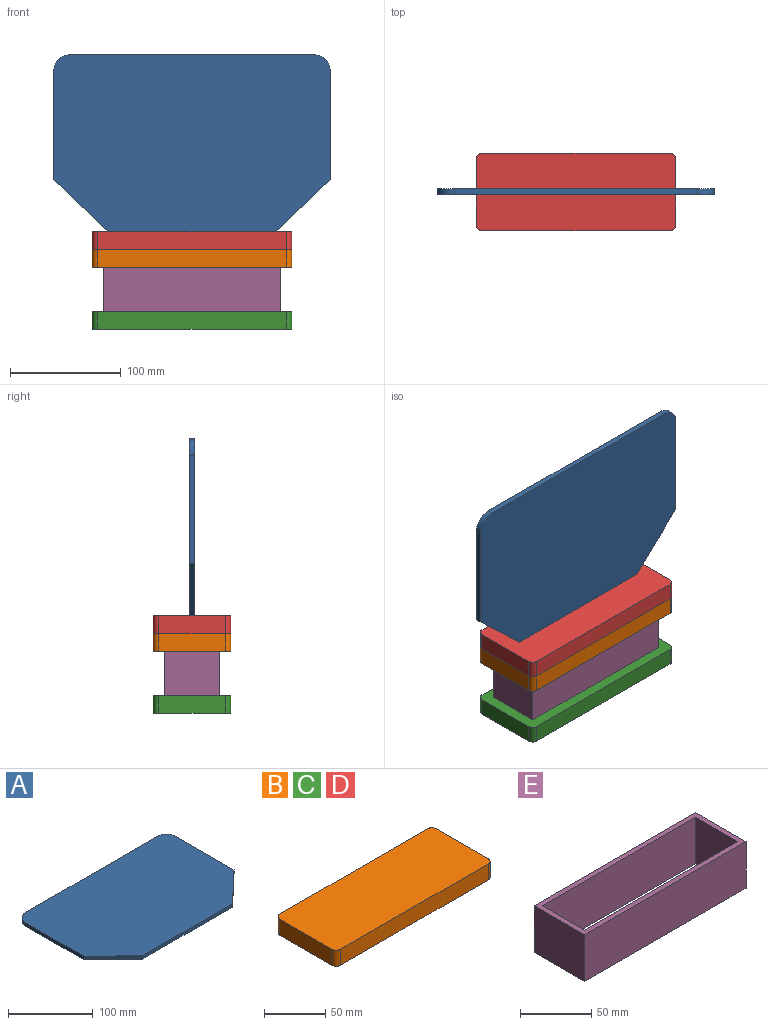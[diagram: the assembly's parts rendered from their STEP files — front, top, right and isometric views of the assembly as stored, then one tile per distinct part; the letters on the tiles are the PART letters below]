
ASSEMBLY  parts=5 mates=4
PART A: 10 faces, bbox 250x160x5 mm
  f0: plane 50x47.5mm, normal (-0.69,-0.72,0), area 344.8mm2, adj f1,f7,f8,f9
  f1: plane 150x5mm, normal (0,-1,0), area 750mm2, adj f0,f2,f8,f9
  f2: plane 50x47.5mm, normal (0.69,-0.72,0), area 344.8mm2, adj f1,f3,f8,f9
  f3: plane 97.5x5mm, normal (1,0,0), area 487.5mm2, adj f2,f4,f8,f9
  f4: cylinder r=15mm len=15mm, axis (0,0,-1), area 117.8mm2, adj f3,f5,f8,f9
  f5: plane 220x5mm, normal (0,1,0), area 1100mm2, adj f4,f6,f8,f9
  f6: cylinder r=15mm len=15mm, axis (0,0,-1), area 117.8mm2, adj f5,f7,f8,f9
  f7: plane 97.5x5mm, normal (-1,0,0), area 487.5mm2, adj f0,f6,f8,f9
  f8: plane 250x160mm, normal (0,0,1), area 37528.3mm2, adj f0,f1,f2,f3,f4,f5,f6,f7
  f9: plane 250x160mm, normal (0,0,-1), area 37528.3mm2, adj f0,f1,f2,f3,f4,f5,f6,f7
PART B: 10 faces, bbox 180x70x16 mm
  f0: plane 60x16mm, normal (-1,0,0), area 960mm2, adj f4,f5,f6,f9
  f1: plane 170x16mm, normal (0,-1,0), area 2720mm2, adj f4,f5,f6,f7
  f2: plane 60x16mm, normal (1,0,0), area 960mm2, adj f4,f5,f7,f8
  f3: plane 170x16mm, normal (0,1,0), area 2720mm2, adj f4,f5,f8,f9
  f4: plane 180x70mm, normal (0,0,1), area 12578.5mm2, adj f0,f1,f2,f3,f6,f7,f8,f9
  f5: plane 180x70mm, normal (0,0,-1), area 12578.5mm2, adj f0,f1,f2,f3,f6,f7,f8,f9
  f6: cylinder r=5mm len=16mm, axis (0,0,1), area 125.7mm2, adj f0,f1,f4,f5
  f7: cylinder r=5mm len=16mm, axis (0,0,-1), area 125.7mm2, adj f1,f2,f4,f5
  f8: cylinder r=5mm len=16mm, axis (0,0,1), area 125.7mm2, adj f2,f3,f4,f5
  f9: cylinder r=5mm len=16mm, axis (0,0,-1), area 125.7mm2, adj f0,f3,f4,f5
PART C: same geometry as B
PART D: same geometry as B
PART E: 10 faces, bbox 160x50x40 mm
  f0: plane 42x40mm, normal (1,0,0), area 1680mm2, adj f1,f7,f8,f9
  f1: plane 152x40mm, normal (0,-1,0), area 6080mm2, adj f0,f2,f8,f9
  f2: plane 42x40mm, normal (-1,0,0), area 1680mm2, adj f1,f7,f8,f9
  f3: plane 50x40mm, normal (-1,0,0), area 2000mm2, adj f4,f6,f8,f9
  f4: plane 160x40mm, normal (0,-1,0), area 6400mm2, adj f3,f5,f8,f9
  f5: plane 50x40mm, normal (1,0,0), area 2000mm2, adj f4,f6,f8,f9
  f6: plane 160x40mm, normal (0,1,0), area 6400mm2, adj f3,f5,f8,f9
  f7: plane 152x40mm, normal (0,1,0), area 6080mm2, adj f0,f2,f8,f9
  f8: plane 160x50mm, normal (0,0,1), area 1616mm2, adj f0,f1,f2,f3,f4,f5,f6,f7
  f9: plane 160x50mm, normal (0,0,-1), area 1616mm2, adj f0,f1,f2,f3,f4,f5,f6,f7
PLACE A rot(axis=(1,0,0),90deg) t=(-125,2.5,89.6)mm
PLACE B t=(-90,-35,56)mm
PLACE C t=(-90,-35,0)mm
PLACE D t=(-90,-35,72)mm
PLACE E t=(-80,-25,16)mm
MATE fastened D.f5 <-> B.f4  axis (0,0,-1) through (0,0,72)mm
MATE fastened E.f9 <-> C.f4  axis (0,0,-1) through (0,0,16)mm
MATE fastened B.f5 <-> E.f8  axis (0,0,-1) through (0,0,56)mm
MATE fastened D.f4 <-> A.f1  axis (0,0,1) through (0,0,88)mm
